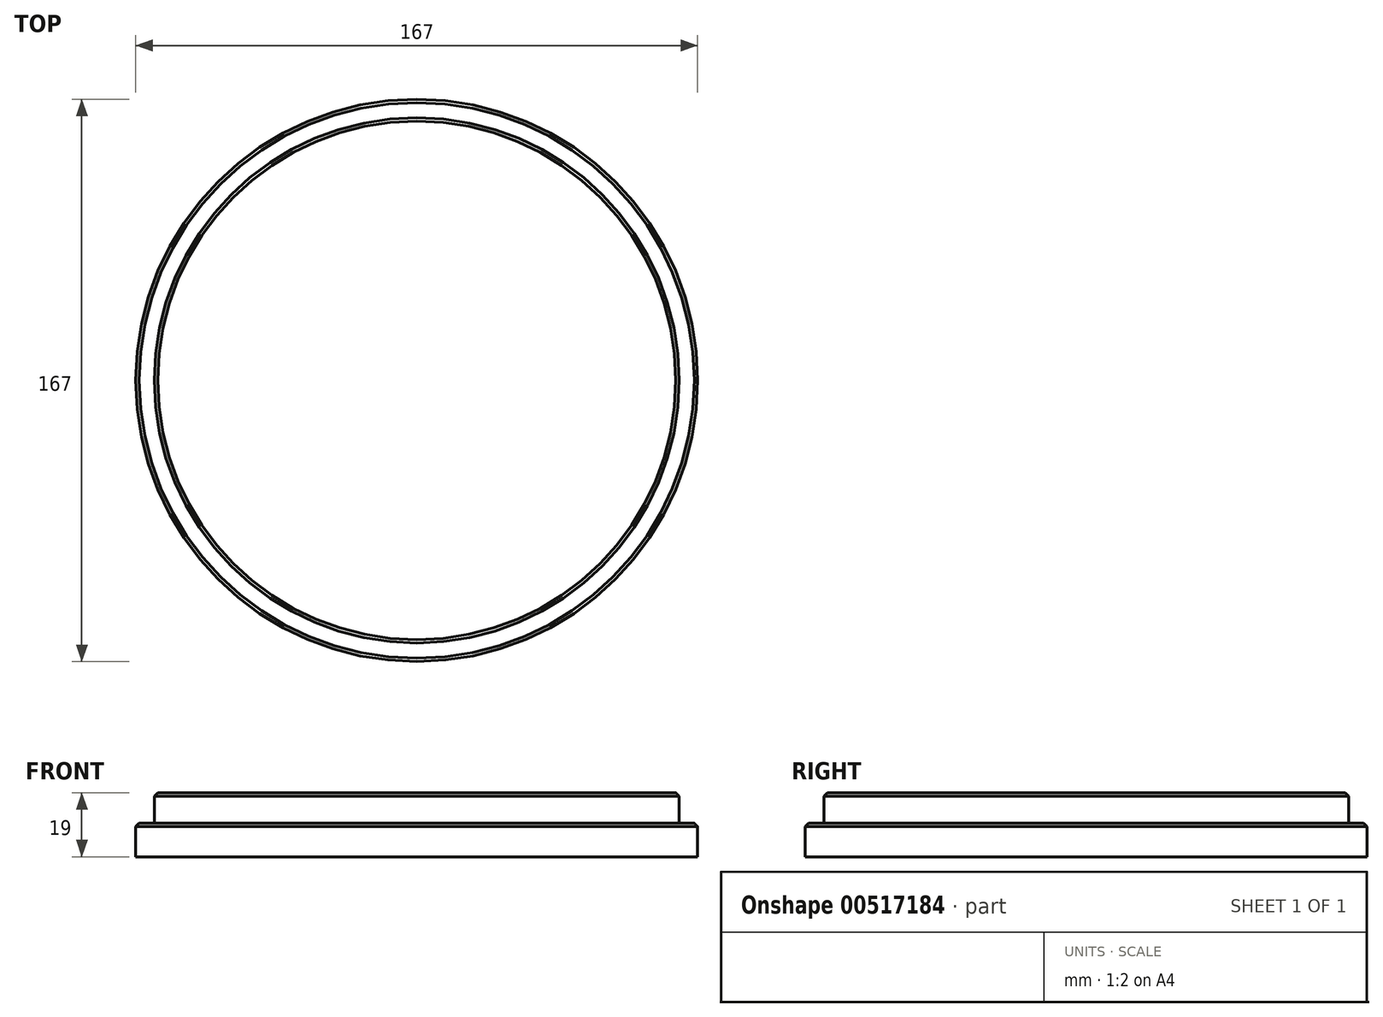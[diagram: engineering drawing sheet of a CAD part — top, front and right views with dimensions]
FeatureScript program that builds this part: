
annotation { "Feature Type Name" : "Feature", "Feature Type Description" : "" }
export const myFeature = defineFeature(function(context is Context, id is Id, definition is map)
    precondition{}
    {
        {
            var Q0;
            Q0=qCreatedBy(makeId("Top.planeOp"),FACE);
            var sketch = newSketch(context, id + "F0", { "sketchPlane" : qUnion([Q0])});
            skCircle(sketch, "E0", {"center": v(0, 0) * mm, "radius": 83.5 * mm});
            skCircle(sketch, "E1", {"center": v(0, 0) * mm, "radius": 78 * mm});
            skSolve(sketch);
        }
        {
            var Q0;
            Q0=makeQuery(id+"F0.imprint","IMPRINT",FACE,{"disambiguationData":[TD([[makeQuery(id+"F0.imprint","IMPRINT",EDGE,{"derivedFrom":sQuery(id+"F0.wireOp",EDGE,"E1")}),1.0]])]});
            extrude(context, id + "F1", {"entities" : qUnion([Q0]), "depth" : 19 * mm, "offsetDistance" : 25 * mm});
        }
        {
            var Q0;
            Q0 = qSketchRegion(id + "F0", true);
            extrude(context, id + "F2", {"entities" : qUnion([Q0]), "operationType" : NewBodyOperationType.ADD, "depth" : 10 * mm, "offsetDistance" : 25 * mm});
        }
        {
            var Q0;
            Q0=makeQuery(id+"F2.opExtrude","CAP_EDGE",EDGE,{"disambiguationData":[OSD([sQuery(id+"F0.wireOp",EDGE,"E0")])],"isStart":false});
            var Q1;
            Q1=makeQuery(id+"F1.opExtrude","CAP_EDGE",EDGE,{"disambiguationData":[OSD([sQuery(id+"F0.wireOp",EDGE,"E1")])],"isStart":false});
            chamfer(context, id + "F3", {"entities" : qUnion([Q0, Q1]), "width" : 1 * mm, "tangentPropagation" : true});
        }
    });
